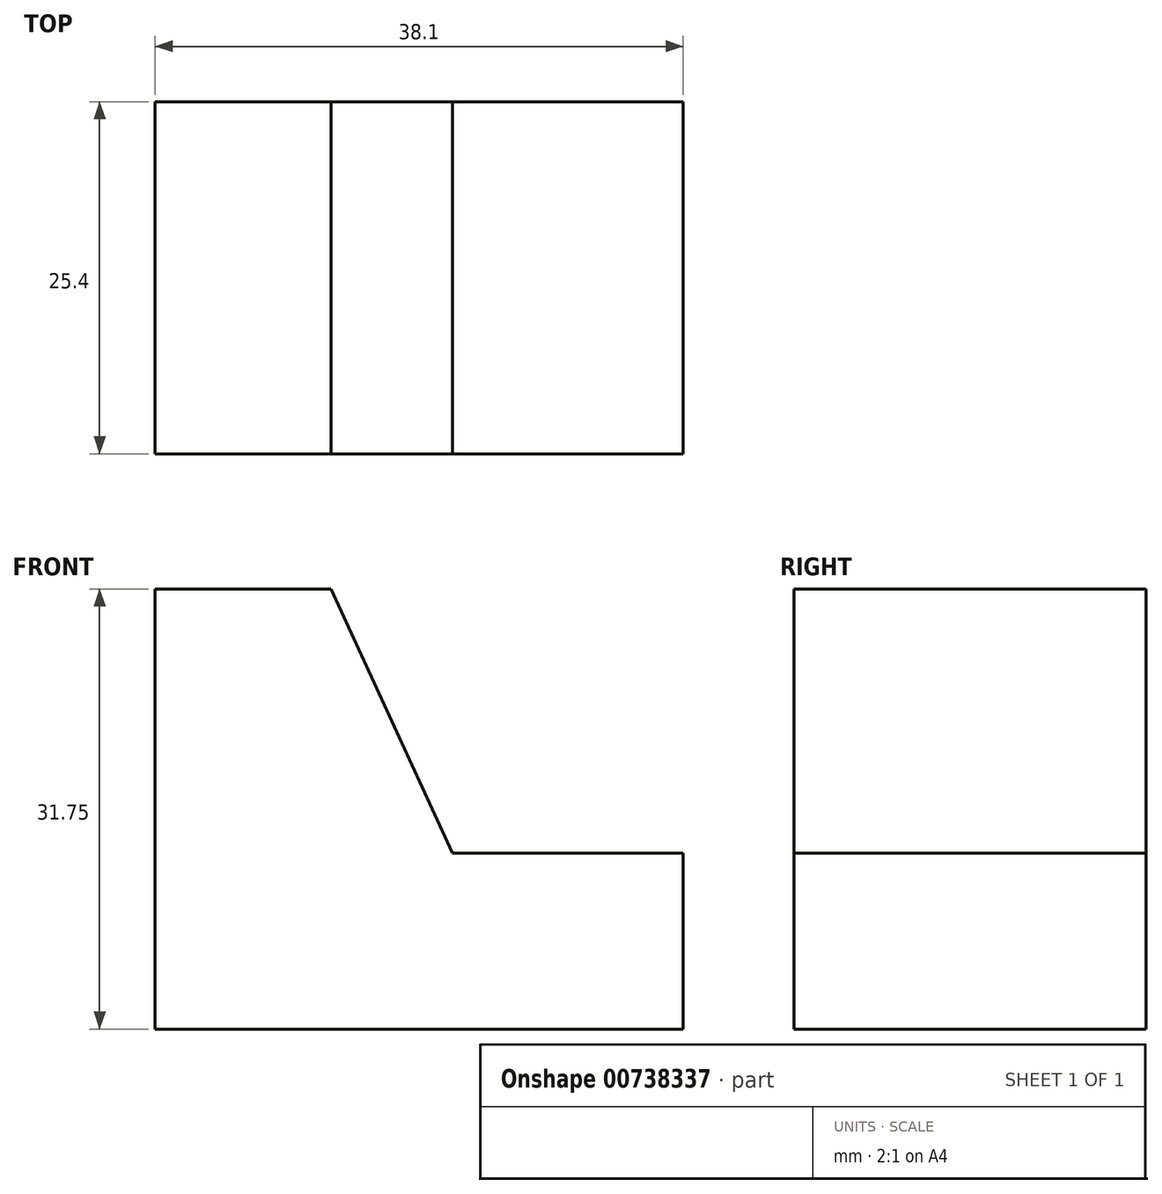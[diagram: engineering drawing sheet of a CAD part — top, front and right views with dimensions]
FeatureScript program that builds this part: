
annotation { "Feature Type Name" : "Feature", "Feature Type Description" : "" }
export const myFeature = defineFeature(function(context is Context, id is Id, definition is map)
    precondition{}
    {
        {
            var Q0;
            Q0=qCreatedBy(makeId("Front.planeOp"),FACE);
            var sketch = newSketch(context, id + "F0", { "sketchPlane" : qUnion([Q0])});
            skLineSegment(sketch, "E0", {"start": v(0, 0) * mm, "end": v(0, 31.75) * mm});
            skLineSegment(sketch, "E1", {"start": v(0, 31.75) * mm, "end": v(12.7, 31.75) * mm});
            skLineSegment(sketch, "E2", {"start": v(12.7, 31.75) * mm, "end": v(21.46, 12.7) * mm});
            skLineSegment(sketch, "E3", {"start": v(21.46, 12.7) * mm, "end": v(38.1, 12.7) * mm});
            skLineSegment(sketch, "E4", {"start": v(38.1, 12.7) * mm, "end": v(38.1, 0) * mm});
            skLineSegment(sketch, "E5", {"start": v(38.1, 0) * mm, "end": v(0, 0) * mm});
            skSolve(sketch);
        }
        {
            var Q0;
            Q0 = qSketchRegion(id + "F0", true);
            extrude(context, id + "F1", {"entities" : qUnion([Q0]), "depth" : 25.4 * mm, "offsetDistance" : 25.4 * mm});
        }
    });
